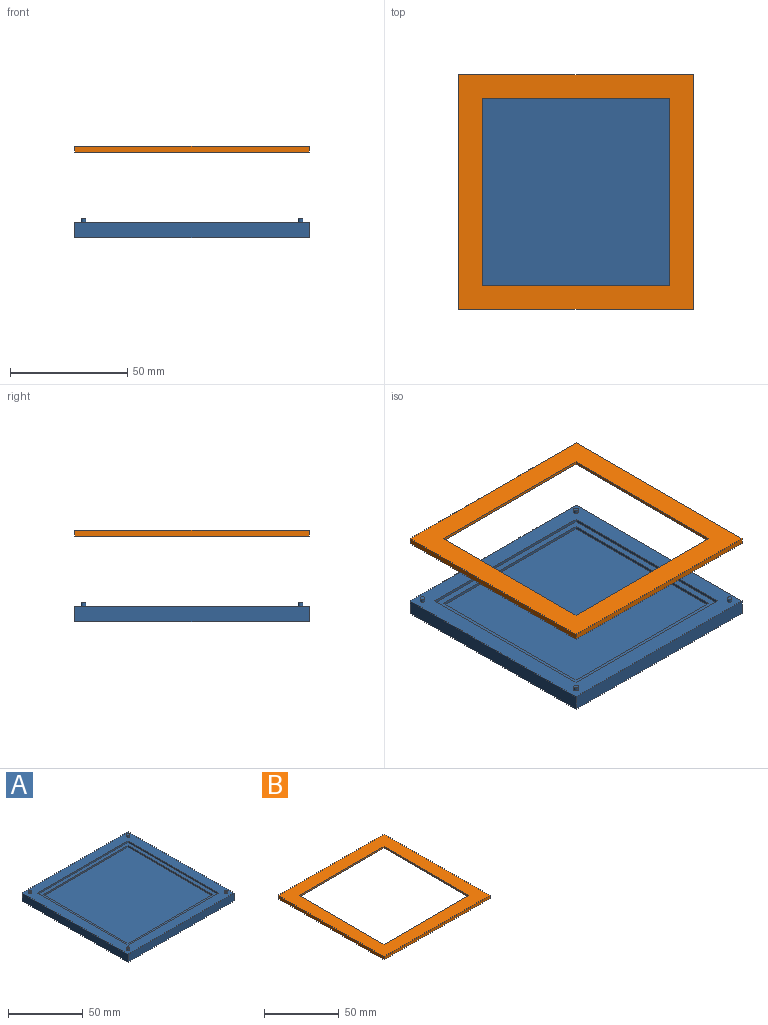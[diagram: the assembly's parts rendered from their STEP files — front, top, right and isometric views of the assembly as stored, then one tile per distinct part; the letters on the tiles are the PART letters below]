
ASSEMBLY  parts=2 mates=1
PART A: 24 faces, bbox 100x100x8 mm
  f0: plane 85x1.25mm, normal (1,0,0), area 106.3mm2, adj f1,f2,f9,f10
  f1: plane 85x1.25mm, normal (0,1,0), area 106.3mm2, adj f0,f3,f9,f10
  f2: plane 85x1.25mm, normal (0,-1,0), area 106.3mm2, adj f0,f3,f9,f10
  f3: plane 85x1.25mm, normal (-1,0,0), area 106.3mm2, adj f1,f2,f9,f10
  f4: plane 80x1.25mm, normal (-1,0,0), area 100mm2, adj f5,f6,f8,f9
  f5: plane 80x1.25mm, normal (0,-1,0), area 100mm2, adj f4,f7,f8,f9
  f6: plane 80x1.25mm, normal (0,1,0), area 100mm2, adj f4,f7,f8,f9
  f7: plane 80x1.25mm, normal (1,0,0), area 100mm2, adj f5,f6,f8,f9
  f8: plane 80x80mm, normal (0,0,1), area 6400mm2, adj f4,f5,f6,f7
  f9: plane 85x85mm, normal (0,0,1), area 825mm2, adj f0,f1,f2,f3,f4,f5,f6,f7
  f10: plane 100x100mm, normal (0,0,1), area 2762.4mm2, adj f0,f1,f2,f3,f12,f13,f14,f15
  f11: plane 100x100mm, normal (0,0,-1), area 10000mm2, adj f12,f13,f14,f15
  f12: plane 100x6.5mm, normal (0,1,0), area 650mm2, adj f10,f11,f13,f15
  f13: plane 100x6.5mm, normal (1,0,0), area 650mm2, adj f10,f11,f12,f14
  f14: plane 100x6.5mm, normal (0,-1,0), area 650mm2, adj f10,f11,f13,f15
  f15: plane 100x6.5mm, normal (-1,0,0), area 650mm2, adj f10,f11,f12,f14
  f16: cylinder r=1mm len=2mm, axis (0,0,-1), area 9.4mm2, adj f10,f17
  f17: plane 2x2mm, normal (0,0,1), area 3.1mm2, adj f16
  f18: cylinder r=1mm len=2mm, axis (0,0,-1), area 9.4mm2, adj f10,f19
  f19: plane 2x2mm, normal (0,0,1), area 3.1mm2, adj f18
  f20: cylinder r=1mm len=2mm, axis (0,0,-1), area 9.4mm2, adj f10,f21
  f21: plane 2x2mm, normal (0,0,1), area 3.1mm2, adj f20
  f22: cylinder r=1mm len=2mm, axis (0,0,-1), area 9.4mm2, adj f10,f23
  f23: plane 2x2mm, normal (0,0,1), area 3.1mm2, adj f22
PART B: 23 faces, bbox 100x100x2.5 mm
  f0: plane 80x1.25mm, normal (0,-1,0), area 100mm2, adj f1,f3,f8,f9
  f1: plane 80x1.25mm, normal (-1,0,0), area 100mm2, adj f0,f2,f3,f9
  f2: plane 80x1.25mm, normal (0,1,0), area 100mm2, adj f1,f3,f8,f9
  f3: plane 100x100mm, normal (0,0,1), area 3600mm2, adj f0,f1,f2,f4,f5,f6,f7,f8
  f4: plane 100x2.5mm, normal (0,1,0), area 250mm2, adj f3,f5,f7,f14
  f5: plane 100x2.5mm, normal (1,0,0), area 250mm2, adj f3,f4,f6,f14
  f6: plane 100x2.5mm, normal (0,-1,0), area 250mm2, adj f3,f5,f7,f14
  f7: plane 100x2.5mm, normal (-1,0,0), area 250mm2, adj f3,f4,f6,f14
  f8: plane 80x1.25mm, normal (1,0,0), area 100mm2, adj f0,f2,f3,f9
  f9: plane 85x85mm, normal (0,0,-1), area 825mm2, adj f0,f1,f2,f8,f10,f11,f12,f13
  f10: plane 85x1.25mm, normal (-1,0,0), area 106.2mm2, adj f9,f11,f12,f14
  f11: plane 85x1.25mm, normal (0,-1,0), area 106.2mm2, adj f9,f10,f13,f14
  f12: plane 85x1.25mm, normal (0,1,0), area 106.2mm2, adj f9,f10,f13,f14
  f13: plane 85x1.25mm, normal (1,0,0), area 106.2mm2, adj f9,f11,f12,f14
  f14: plane 100x100mm, normal (0,0,-1), area 2762.4mm2, adj f4,f5,f6,f7,f10,f11,f12,f13
  f15: cylinder r=1mm len=2mm, axis (0,0,-1), area 9.4mm2, adj f14,f16
  f16: plane 2x2mm, normal (0,0,-1), area 3.1mm2, adj f15
  f17: cylinder r=1mm len=2mm, axis (0,0,-1), area 9.4mm2, adj f14,f18
  f18: plane 2x2mm, normal (0,0,-1), area 3.1mm2, adj f17
  f19: cylinder r=1mm len=2mm, axis (0,0,-1), area 9.4mm2, adj f14,f20
  f20: plane 2x2mm, normal (0,0,-1), area 3.1mm2, adj f19
  f21: cylinder r=1mm len=2mm, axis (0,0,-1), area 9.4mm2, adj f14,f22
  f22: plane 2x2mm, normal (0,0,-1), area 3.1mm2, adj f21
PLACE A t=(-87.39,-72.9,159.78)mm
PLACE B t=(-87.39,-72.9,164.78)mm
MATE slider A.f10 <-> B.f14  axis (0,0,1) through (-87.39,27.1,159.78)mm
